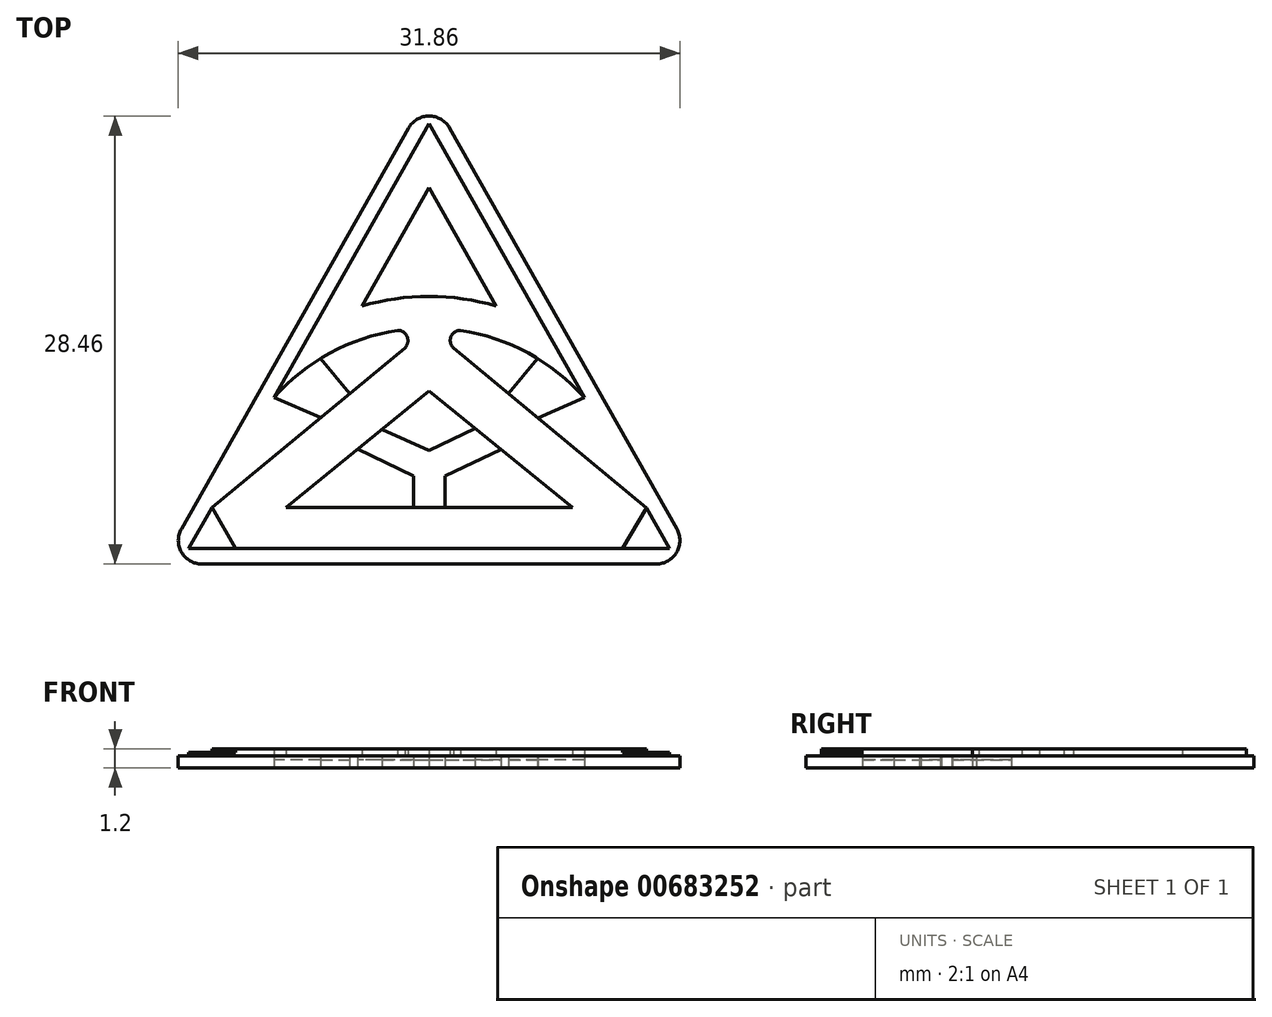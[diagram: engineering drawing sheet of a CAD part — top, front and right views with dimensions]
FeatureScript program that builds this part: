
annotation { "Feature Type Name" : "Feature", "Feature Type Description" : "" }
export const myFeature = defineFeature(function(context is Context, id is Id, definition is map)
    precondition{}
    {
        {
            var Q0;
            Q0=qCreatedBy(makeId("Top.planeOp"),FACE);
            var sketch = newSketch(context, id + "F0", { "sketchPlane" : qUnion([Q0])});
            skLineSegment(sketch, "E0", {"start": v(0, 30) * mm, "end": v(-17, 0) * mm});
            skLineSegment(sketch, "E1", {"start": v(-17, 0) * mm, "end": v(17, 0) * mm});
            skLineSegment(sketch, "E2", {"start": v(17, 0) * mm, "end": v(0, 30) * mm});
            skLineSegment(sketch, "E3", {"start": v(0, 27.97) * mm, "end": v(9.86, 10.57) * mm});
            skLineSegment(sketch, "E4", {"start": v(0, 27.97) * mm, "end": v(-9.86, 10.57) * mm});
            skArc(sketch, "E5", {"start": v(9.86, 10.57) * mm, "mid": v(6.3, 13.4) * mm, "end": v(2, 14.85) * mm});
            skLineSegment(sketch, "E6", {"start": v(0, 23.91) * mm, "end": v(-4.26, 16.39) * mm});
            skLineSegment(sketch, "E7", {"start": v(0, 23.91) * mm, "end": v(4.26, 16.39) * mm});
            skArc(sketch, "E8", {"start": v(4.26, 16.39) * mm, "mid": v(0, 17) * mm, "end": v(-4.26, 16.39) * mm});
            skLineSegment(sketch, "E9", {"start": v(-15.28, 1) * mm, "end": v(-13.78, 3.6) * mm});
            skLineSegment(sketch, "E10", {"start": v(-13.78, 3.6) * mm, "end": v(-12.28, 1) * mm});
            skLineSegment(sketch, "E11", {"start": v(-12.28, 1) * mm, "end": v(-15.28, 1) * mm});
            skLineSegment(sketch, "E12", {"start": v(15.28, 1) * mm, "end": v(13.83, 3.57) * mm});
            skLineSegment(sketch, "E13", {"start": v(13.83, 3.57) * mm, "end": v(12.28, 1) * mm});
            skLineSegment(sketch, "E14", {"start": v(12.28, 1) * mm, "end": v(15.28, 1) * mm});
            skLineSegment(sketch, "E15", {"start": v(-9.1, 3.6) * mm, "end": v(9.12, 3.58) * mm});
            skLineSegment(sketch, "E16", {"start": v(-12.28, 1) * mm, "end": v(12.28, 1) * mm});
            skLineSegment(sketch, "E17", {"start": v(-13.78, 3.6) * mm, "end": v(-1.54, 13.73) * mm});
            skLineSegment(sketch, "E18", {"start": v(1.54, 13.73) * mm, "end": v(13.83, 3.57) * mm});
            skLineSegment(sketch, "E19", {"start": v(9.12, 3.58) * mm, "end": v(0, 11) * mm});
            skLineSegment(sketch, "E20", {"start": v(0, 11) * mm, "end": v(-9.1, 3.6) * mm});
            skLineSegment(sketch, "E21", {"start": v(-6.9, 9.3) * mm, "end": v(-9.86, 10.57) * mm});
            skLineSegment(sketch, "E22", {"start": v(9.86, 10.57) * mm, "end": v(6.91, 9.29) * mm});
            skLineSegment(sketch, "E23", {"start": v(-6.9, 13.06) * mm, "end": v(-5.05, 10.83) * mm});
            skLineSegment(sketch, "E24", {"start": v(6.9, 13.06) * mm, "end": v(5.05, 10.83) * mm});
            skLineSegment(sketch, "E25", {"start": v(-1, 3.59) * mm, "end": v(-1, 5.59) * mm});
            skLineSegment(sketch, "E26", {"start": v(1, 5.58) * mm, "end": v(1, 3.58) * mm});
            skLineSegment(sketch, "E27", {"start": v(-1, 5.59) * mm, "end": v(-4.55, 7.3) * mm});
            skLineSegment(sketch, "E28", {"start": v(1, 5.58) * mm, "end": v(4.56, 7.29) * mm});
            skLineSegment(sketch, "E29", {"start": v(-3, 8.56) * mm, "end": v(0, 7.21) * mm});
            skLineSegment(sketch, "E30", {"start": v(0, 7.21) * mm, "end": v(2.93, 8.62) * mm});
            skArc(sketch, "E31", {"start": v(-1.54, 13.73) * mm, "mid": v(-1.4, 14.44) * mm, "end": v(-2, 14.85) * mm});
            skArc(sketch, "E32", {"start": v(2, 14.85) * mm, "mid": v(1.4, 14.44) * mm, "end": v(1.54, 13.73) * mm});
            skArc(sketch, "E33.trimOffspring", {"start": v(-2, 14.85) * mm, "mid": v(-6.3, 13.4) * mm, "end": v(-9.86, 10.57) * mm});
            skPoint(sketch, "E34.orphan", {"position": v(0, 15) * mm});
            skSolve(sketch);
        }
        {
            var Q0;
            Q0=makeQuery(id+"F0.imprint","IMPRINT",FACE,{"disambiguationData":[TD([[makeQuery(id+"F0.imprint","IMPRINT",EDGE,{"derivedFrom":sQuery(id+"F0.wireOp",EDGE,"E0")}),1.0]])]});
            var Q1;
            Q1=makeQuery(id+"F0.imprint","IMPRINT",FACE,{"disambiguationData":[TD([[makeQuery(id+"F0.imprint","IMPRINT",EDGE,{"derivedFrom":sQuery(id+"F0.wireOp",EDGE,"E6")}),1.0]])]});
            var Q2;
            {var subQ3=sQuery(id+"F0.wireOp",EDGE,"E23");Q2=makeQuery(id+"F0.imprint","IMPRINT",FACE,{"disambiguationData":[TD([[makeQuery(id+"F0.imprint","IMPRINT",EDGE,{"derivedFrom":subQ3}),1.0]])]});}
            var Q3;
            {var subQ3=sQuery(id+"F0.wireOp",EDGE,"E24");Q3=makeQuery(id+"F0.imprint","IMPRINT",FACE,{"disambiguationData":[TD([[makeQuery(id+"F0.imprint","IMPRINT",EDGE,{"derivedFrom":subQ3}),-1.0]])]});}
            var Q4;
            {var subQ4=sQuery(id+"F0.wireOp",EDGE,"E29");Q4=makeQuery(id+"F0.imprint","IMPRINT",FACE,{"disambiguationData":[TD([[makeQuery(id+"F0.imprint","IMPRINT",EDGE,{"derivedFrom":subQ4}),1.0]])]});}
            var Q5;
            {var subQ3=sQuery(id+"F0.wireOp",EDGE,"E25");Q5=makeQuery(id+"F0.imprint","IMPRINT",FACE,{"disambiguationData":[TD([[makeQuery(id+"F0.imprint","IMPRINT",EDGE,{"derivedFrom":subQ3}),1.0]])]});}
            var Q6;
            {var subQ3=sQuery(id+"F0.wireOp",EDGE,"E26");Q6=makeQuery(id+"F0.imprint","IMPRINT",FACE,{"disambiguationData":[TD([[makeQuery(id+"F0.imprint","IMPRINT",EDGE,{"derivedFrom":subQ3}),1.0]])]});}
            extrude(context, id + "F1", {"entities" : qUnion([Q0, Q1, Q2, Q3, Q4, Q5, Q6]), "depth" : 0.75 * mm, "offsetDistance" : 25 * mm});
        }
        {
            var Q0;
            {var subQ3=sQuery(id+"F0.wireOp",EDGE,"E3");Q0=makeQuery(id+"F0.imprint","IMPRINT",FACE,{"disambiguationData":[TD([[makeQuery(id+"F0.imprint","IMPRINT",EDGE,{"derivedFrom":subQ3}),-1.0]])]});}
            extrude(context, id + "F2", {"entities" : qUnion([Q0]), "operationType" : NewBodyOperationType.ADD, "depth" : 1.2 * mm, "offsetDistance" : 25 * mm});
        }
        {
            var Q0;
            {var subQ0=sQuery(id+"F0.wireOp",EDGE,"E21");Q0=makeQuery(id+"F0.imprint","IMPRINT",FACE,{"disambiguationData":[TD([[makeQuery(id+"F0.imprint","IMPRINT",EDGE,{"derivedFrom":subQ0}),-1.0]])]});}
            var Q1;
            {var subQ0=sQuery(id+"F0.wireOp",EDGE,"E25");Q1=makeQuery(id+"F0.imprint","IMPRINT",FACE,{"disambiguationData":[TD([[makeQuery(id+"F0.imprint","IMPRINT",EDGE,{"derivedFrom":subQ0}),-1.0]])]});}
            var Q2;
            {var subQ0=sQuery(id+"F0.wireOp",EDGE,"E22");Q2=makeQuery(id+"F0.imprint","IMPRINT",FACE,{"disambiguationData":[TD([[makeQuery(id+"F0.imprint","IMPRINT",EDGE,{"derivedFrom":subQ0}),-1.0]])]});}
            extrude(context, id + "F3", {"entities" : qUnion([Q0, Q1, Q2]), "depth" : 0.5 * mm, "offsetDistance" : 25 * mm});
        }
        {
            var Q0;
            Q0=makeQuery(id+"F1.opExtrude","SWEPT_EDGE",EDGE,{"disambiguationData":[OSD([sQuery(id+"F0.wireOp",EDGE,"E0"),sQuery(id+"F0.wireOp",EDGE,"E2")])]});
            var Q1;
            Q1=makeQuery(id+"F1.opExtrude","SWEPT_EDGE",EDGE,{"disambiguationData":[OSD([sQuery(id+"F0.wireOp",EDGE,"E0"),sQuery(id+"F0.wireOp",EDGE,"E1")])]});
            var Q2;
            Q2=makeQuery(id+"F1.opExtrude","SWEPT_EDGE",EDGE,{"disambiguationData":[OSD([sQuery(id+"F0.wireOp",EDGE,"E1"),sQuery(id+"F0.wireOp",EDGE,"E2")])]});
            fillet(context, id + "F4", {"entities" : qUnion([Q0, Q1, Q2]), "radius" : 1.5 * mm, "tangentPropagation" : true, "allowEdgeOverflow" : false});
        }
        {
            var Q0;
            Q0=makeQuery(id+"F0.imprint","IMPRINT",FACE,{"disambiguationData":[TD([[makeQuery(id+"F0.imprint","IMPRINT",EDGE,{"derivedFrom":sQuery(id+"F0.wireOp",EDGE,"E9")}),-1.0]])]});
            var Q1;
            Q1=makeQuery(id+"F0.imprint","IMPRINT",FACE,{"disambiguationData":[TD([[makeQuery(id+"F0.imprint","IMPRINT",EDGE,{"derivedFrom":sQuery(id+"F0.wireOp",EDGE,"E12")}),1.0]])]});
            extrude(context, id + "F5", {"entities" : qUnion([Q0, Q1]), "operationType" : NewBodyOperationType.ADD, "depth" : 1 * mm, "offsetDistance" : 25 * mm});
        }
    });
